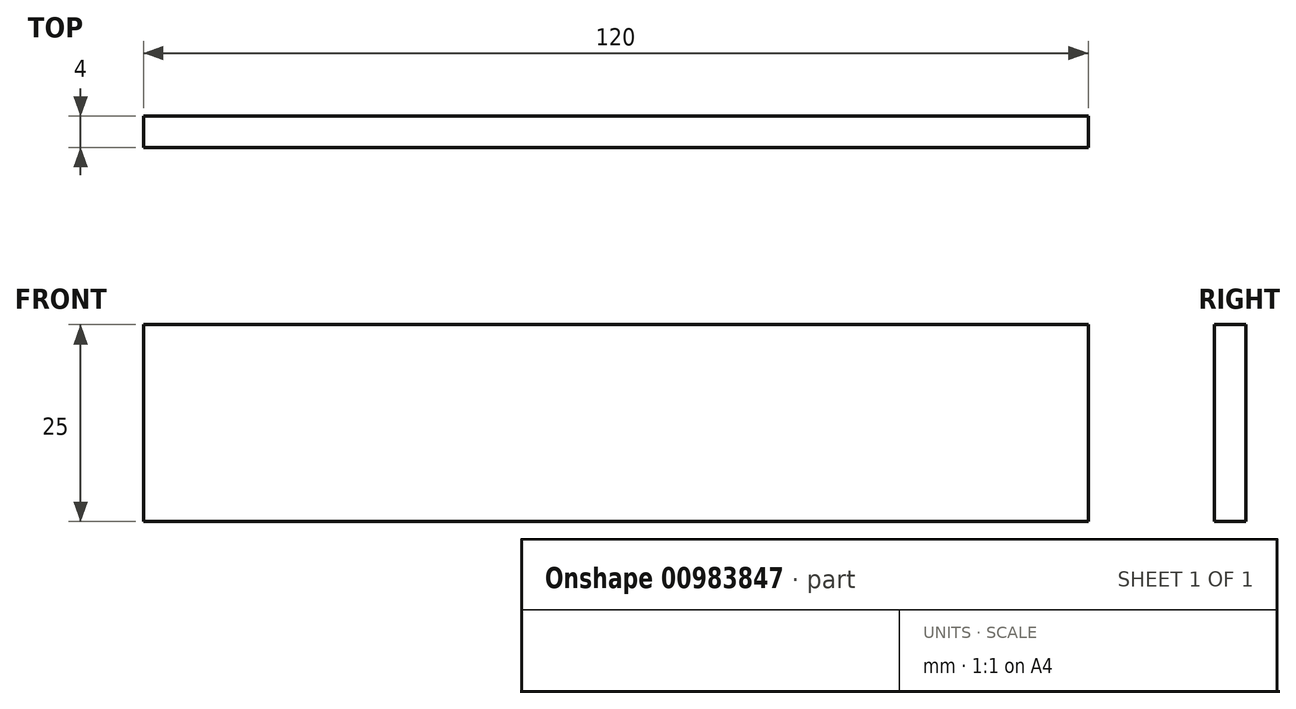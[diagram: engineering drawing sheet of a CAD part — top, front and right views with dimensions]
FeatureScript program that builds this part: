
annotation { "Feature Type Name" : "Feature", "Feature Type Description" : "" }
export const myFeature = defineFeature(function(context is Context, id is Id, definition is map)
    precondition{}
    {
        {
            var Q0;
            Q0=qCreatedBy(makeId("Front.planeOp"),FACE);
            var sketch = newSketch(context, id + "F0", { "sketchPlane" : qUnion([Q0])});
            skLineSegment(sketch, "E0.bottom", {"start": v(-34.46, 17.4) * mm, "end": v(85.54, 17.4) * mm});
            skLineSegment(sketch, "E0.top", {"start": v(-34.46, -7.6) * mm, "end": v(85.54, -7.6) * mm});
            skLineSegment(sketch, "E0.left", {"start": v(-34.46, 17.4) * mm, "end": v(-34.46, -7.6) * mm});
            skLineSegment(sketch, "E0.right", {"start": v(85.54, 17.4) * mm, "end": v(85.54, -7.6) * mm});
            skSolve(sketch);
        }
        {
            var Q0;
            Q0=makeQuery(id+"F0.imprint","IMPRINT",FACE,{"disambiguationData":[TD([[makeQuery(id+"F0.imprint","IMPRINT",EDGE,{"derivedFrom":sQuery(id+"F0.wireOp",EDGE,"E0.bottom")}),-1.0]])]});
            extrude(context, id + "F1", {"entities" : qUnion([Q0]), "depth" : 4 * mm, "offsetDistance" : 25 * mm});
        }
    });
